# Revit family: TINO-xxFWSxxxFx
name_source: partatom
category: Leuchten
units: mm (PartAtom-declared; Revit-internal decimal feet)

## family parameters
Basisbauteil = Fläche
Beim Laden mit Abzugskörper schneiden = Nein
Bemaßung runder Anschluss = Durchmesser verwenden
Gemeinsam genutzt = Nein
Lichtquelle = Ja
OmniClass-Nummer = 23.80.70.11
OmniClass-Titel = Luminaries for Internal Lighting
Raumberechnungspunkt = Nein
Teiletyp = Normal

## types (6) — shared parameters
Baugruppenkennzeichen = D5020200
Datei für fotometrisches Netz = TINO DAFWS840F0300.IES
Emissionsform beim Rendern sichtbar = Nein
Farbfilter = 16777215
Farbtemperaturverschiebung bei Dämpfen der Lampe = <Keine Auswahl>
Hersteller = RIDI Leuchten GmbH
Lampe = LED
Neigungswinkel = 90.00°
URL = www.ridi.de
Von Kreisdurchmesser aussenden = 65 mm  [stored 0.213255 ft]
brand = RIDI
conformity mark = CE
electrical safety class = 1
height = 195 mm  [stored 0.639764 ft]
ingress protection (IP) code = IP20
length = 265 mm  [stored 0.869423 ft]
nominal frequency = 50-60Hz
nominal voltage = 230
voltage type (AC, DC, UC) = AC
weight = 0,89 kg
width = 92 mm  [stored 0.301837 ft]
zero-valued in all types: Vorgabe-Ansicht

## per-type parameters (varying)
| type | Modell | Scheinlast | rated input power |
| TINO NDFWS830F0300 | 0326735AH | 22 VA | 22 |
| TINO DAFWS830F0300 | 0336735AH | 22 VA | 22 |
| TINO NDFWS840F0300 | 0326739AH | 22 VA | 22 |
| TINO DAFWS840F0300 | 0336739AH | 22 VA | 22 |
| TINO DAFWS930F0250 | 0336743AH | 20 VA | 20 |
| TINO NDFWS930F0250 | 0326743AH | 20 VA | 20 |

note: column(s) folded — value = type name in every type: product name

note: [stored X ft] marks values corroborated as IEEE doubles in the binary element streams (Revit-internal decimal feet)
